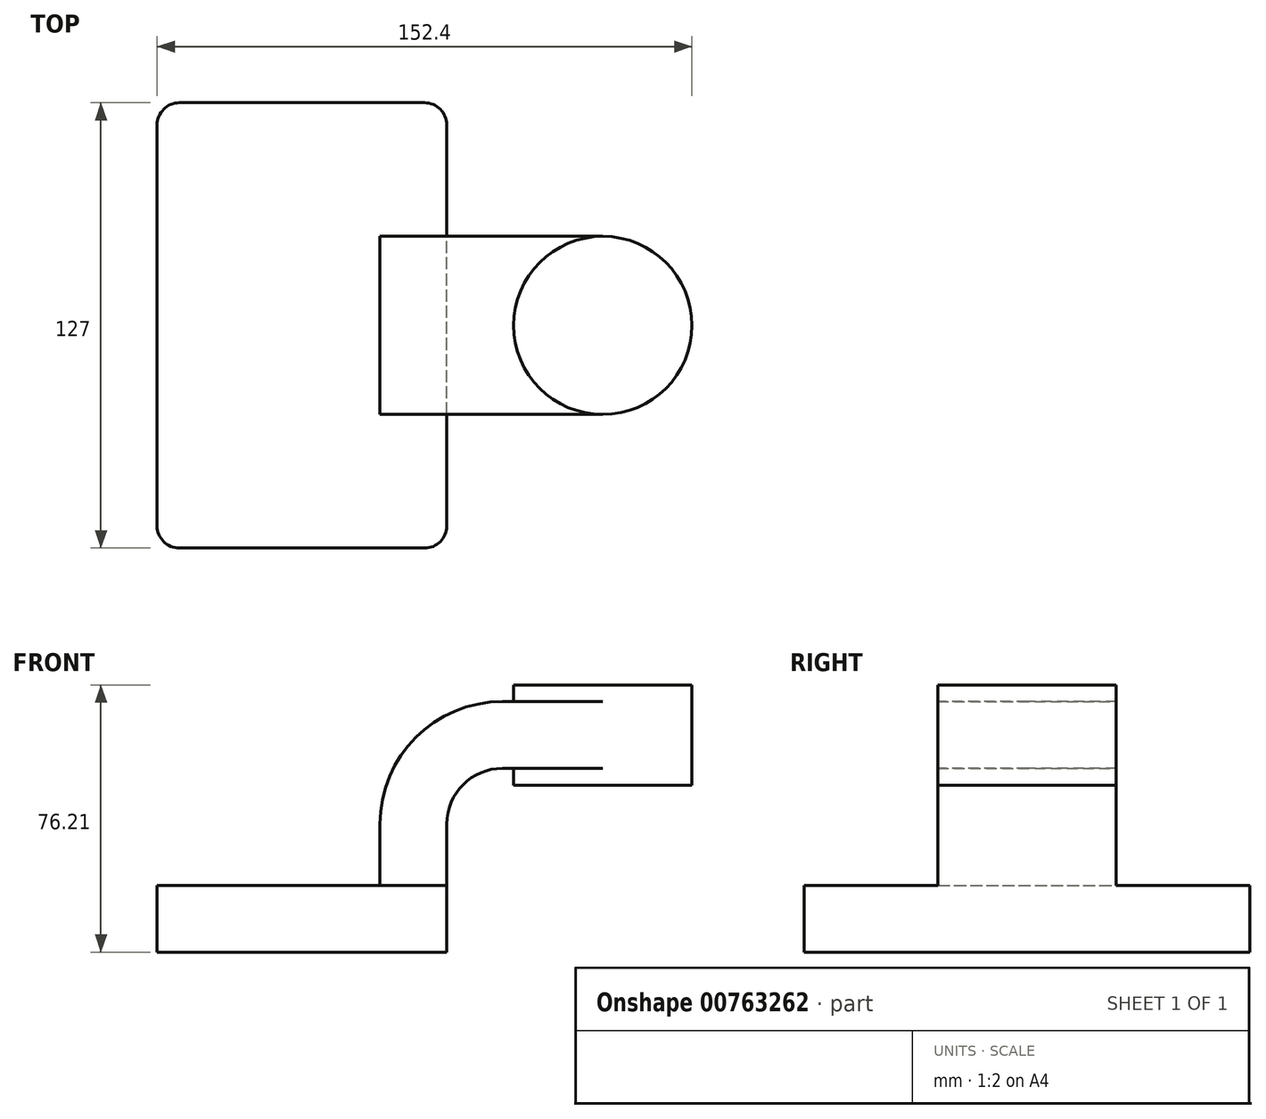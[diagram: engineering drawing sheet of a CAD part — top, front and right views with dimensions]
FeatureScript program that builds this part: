
annotation { "Feature Type Name" : "Feature", "Feature Type Description" : "" }
export const myFeature = defineFeature(function(context is Context, id is Id, definition is map)
    precondition{}
    {
        {
            var Q0;
            Q0=qCreatedBy(makeId("Front.planeOp"),FACE);
            var sketch = newSketch(context, id + "F0", { "sketchPlane" : qUnion([Q0])});
            skLineSegment(sketch, "E0.bottom", {"start": v(-41.28, 9.52) * mm, "end": v(41.28, 9.53) * mm});
            skLineSegment(sketch, "E0.top", {"start": v(-41.28, -9.53) * mm, "end": v(41.28, -9.53) * mm});
            skLineSegment(sketch, "E0.left", {"start": v(-41.28, 9.52) * mm, "end": v(-41.28, -9.53) * mm});
            skLineSegment(sketch, "E0.right", {"start": v(41.28, 9.53) * mm, "end": v(41.28, -9.52) * mm});
            skPoint(sketch, "E0.middle", {"position": v(0, 0) * mm});
            skLineSegment(sketch, "E1.bottom", {"start": v(60.32, 66.67) * mm, "end": v(111.12, 66.67) * mm});
            skLineSegment(sketch, "E1.top", {"start": v(60.32, 38.1) * mm, "end": v(111.12, 38.1) * mm});
            skLineSegment(sketch, "E1.left", {"start": v(60.32, 66.67) * mm, "end": v(60.32, 38.1) * mm});
            skLineSegment(sketch, "E1.right", {"start": v(111.12, 66.67) * mm, "end": v(111.12, 38.1) * mm});
            skPoint(sketch, "E1.middle", {"position": v(85.72, 52.39) * mm});
            skLineSegment(sketch, "E2", {"start": v(41.27, 9.53) * mm, "end": v(41.27, 27) * mm});
            skArc(sketch, "E3", {"start": v(41.27, 27) * mm, "mid": v(45.92, 38.23) * mm, "end": v(57.15, 42.88) * mm});
            skLineSegment(sketch, "E4", {"start": v(57.15, 42.88) * mm, "end": v(85.86, 42.88) * mm});
            skLineSegment(sketch, "E5.0", {"start": v(57.15, 61.93) * mm, "end": v(85.72, 61.93) * mm});
            skArc(sketch, "E5.1", {"start": v(22.22, 27) * mm, "mid": v(32.45, 51.7) * mm, "end": v(57.15, 61.93) * mm});
            skLineSegment(sketch, "E5.2", {"start": v(22.23, 9.53) * mm, "end": v(22.23, 27) * mm});
            skLineSegment(sketch, "E6", {"start": v(85.72, 38.1) * mm, "end": v(85.72, 66.68) * mm});
            skFitSpline(sketch, "E7", {"points": [v(-41.28, 9.53) * mm, v(57.15, 61.93) * mm], "startDerivative": vector(39.32, 80.27) * mm, "endDerivative": vector(120.75, -6.9) * mm});
            skSolve(sketch);
        }
        {
            var Q0;
            Q0=makeQuery(id+"F0.imprint","IMPRINT",FACE,{"disambiguationData":[TD([[makeQuery(id+"F0.imprint","IMPRINT",EDGE,{"derivedFrom":sQuery(id+"F0.wireOp",EDGE,"E0.top")}),1.0]])]});
            extrude(context, id + "F1", {"entities" : qUnion([Q0]), "endBound" : BoundingType.SYMMETRIC, "depth" : 127 * mm, "offsetDistance" : 25.4 * mm});
        }
        {
            var Q0;
            {var subQ1=sQuery(id+"F0.wireOp",EDGE,"E2");Q0=makeQuery(id+"F0.imprint","IMPRINT",FACE,{"disambiguationData":[TD([[makeQuery(id+"F0.imprint","IMPRINT",EDGE,{"derivedFrom":subQ1}),1.0]])]});}
            var Q1;
            {var subQ0=sQuery(id+"F0.wireOp",EDGE,"E5.0");var subQ1=sQuery(id+"F0.wireOp",EDGE,"E1.left");var subQ2=makeQuery(id+"F0.imprint","INTERSECT",VERTEX,{"derivedFrom":[subQ1,subQ0]});Q1=makeQuery(id+"F0.imprint","IMPRINT",FACE,{"disambiguationData":[TD([[makeQuery(id+"F0.imprint","IMPRINT",EDGE,{"disambiguationData":[TD([[subQ2,-1.0]])],"derivedFrom":subQ1}),1.0]])]});}
            extrude(context, id + "F2", {"entities" : qUnion([Q0, Q1]), "operationType" : NewBodyOperationType.ADD, "endBound" : BoundingType.SYMMETRIC, "depth" : 50.8 * mm, "offsetDistance" : 25.4 * mm});
        }
        {
            var Q0;
            Q0=makeQuery(id+"F0.imprint","IMPRINT",FACE,{"disambiguationData":[TD([[makeQuery(id+"F0.imprint","IMPRINT",EDGE,{"derivedFrom":sQuery(id+"F0.wireOp",EDGE,"E5.1")}),1.0]])]});
            extrude(context, id + "F3", {"entities" : qUnion([Q0]), "operationType" : NewBodyOperationType.ADD, "endBound" : BoundingType.SYMMETRIC, "depth" : 15.88 * mm, "offsetDistance" : 25.4 * mm});
        }
        {
            var Q0;
            {var subQ0=sQuery(id+"F0.wireOp",EDGE,"E1.right");Q0=makeQuery(id+"F0.imprint","IMPRINT",FACE,{"disambiguationData":[TD([[makeQuery(id+"F0.imprint","IMPRINT",EDGE,{"derivedFrom":subQ0}),-1.0]])]});}
            var Q1;
            Q1=sQuery(id+"F0.wireOp",EDGE,"E6");
            revolve(context, id + "F4", {"operationType" : NewBodyOperationType.ADD, "surfaceOperationType" : NewSurfaceOperationType.NEW, "entities" : qUnion([Q0]), "axis" : qUnion([Q1]), "revolveType" : RevolveType.FULL});
        }
        {
            var Q0;
            Q0=makeQuery(id+"F1.opExtrude","CAP_EDGE",EDGE,{"disambiguationData":[OSD([sQuery(id+"F0.wireOp",EDGE,"E0.left")])],"isStart":false});
            var Q1;
            Q1=makeQuery(id+"F1.opExtrude","CAP_EDGE",EDGE,{"disambiguationData":[OSD([sQuery(id+"F0.wireOp",EDGE,"E0.right")])],"isStart":false});
            var Q2;
            Q2=makeQuery(id+"F1.opExtrude","CAP_EDGE",EDGE,{"disambiguationData":[OSD([sQuery(id+"F0.wireOp",EDGE,"E0.left")])],"isStart":true});
            var Q3;
            Q3=makeQuery(id+"F1.opExtrude","CAP_EDGE",EDGE,{"disambiguationData":[OSD([sQuery(id+"F0.wireOp",EDGE,"E0.right")])],"isStart":true});
            fillet(context, id + "F5", {"entities" : qUnion([Q0, Q1, Q2, Q3]), "radius" : 6.35 * mm, "tangentPropagation" : true, "allowEdgeOverflow" : false});
        }
    });
